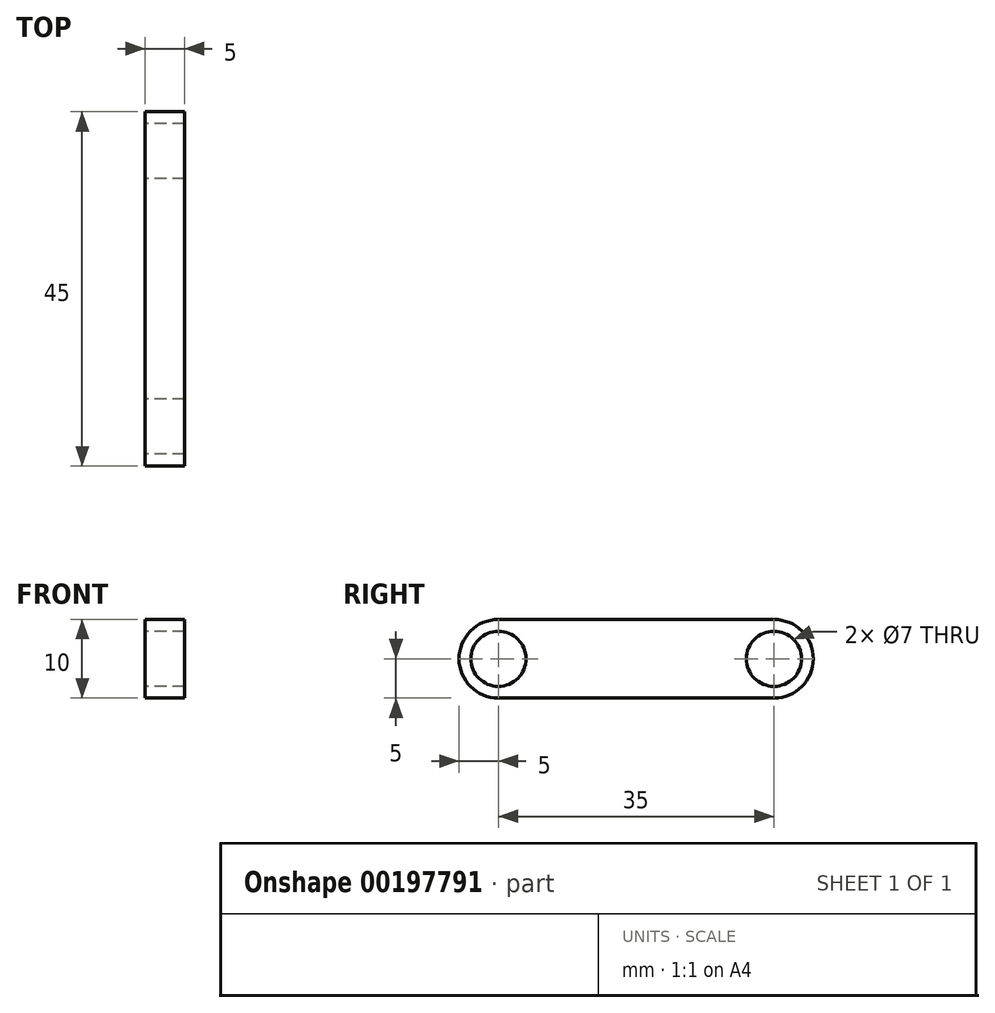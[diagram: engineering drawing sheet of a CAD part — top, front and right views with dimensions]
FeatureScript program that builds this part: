
annotation { "Feature Type Name" : "Feature", "Feature Type Description" : "" }
export const myFeature = defineFeature(function(context is Context, id is Id, definition is map)
    precondition{}
    {
        {
            var Q0;
            Q0=qCreatedBy(makeId("Right.planeOp"),FACE);
            var sketch = newSketch(context, id + "F0", { "sketchPlane" : qUnion([Q0])});
            skLineSegment(sketch, "E0.bottom", {"start": v(17.5, 5) * mm, "end": v(-17.5, 5) * mm});
            skLineSegment(sketch, "E0.top", {"start": v(17.5, -5) * mm, "end": v(-17.5, -5) * mm});
            skLineSegment(sketch, "E0.left", {"start": v(17.5, 5) * mm, "end": v(17.5, -5) * mm});
            skLineSegment(sketch, "E0.right", {"start": v(-17.5, 5) * mm, "end": v(-17.5, -5) * mm});
            skPoint(sketch, "E0.middle", {"position": v(0, 0) * mm});
            skCircle(sketch, "E1", {"center": v(-17.5, 0) * mm, "radius": 5 * mm});
            skCircle(sketch, "E2", {"center": v(17.5, 0) * mm, "radius": 5 * mm});
            skCircle(sketch, "E3", {"center": v(-17.5, 0) * mm, "radius": 3.5 * mm});
            skCircle(sketch, "E4", {"center": v(17.5, 0) * mm, "radius": 3.5 * mm});
            skSolve(sketch);
        }
        {
            var Q0;
            Q0 = qSketchRegion(id + "F0", true);
            extrude(context, id + "F1", {"entities" : qUnion([Q0]), "depth" : 5 * mm});
        }
    });
